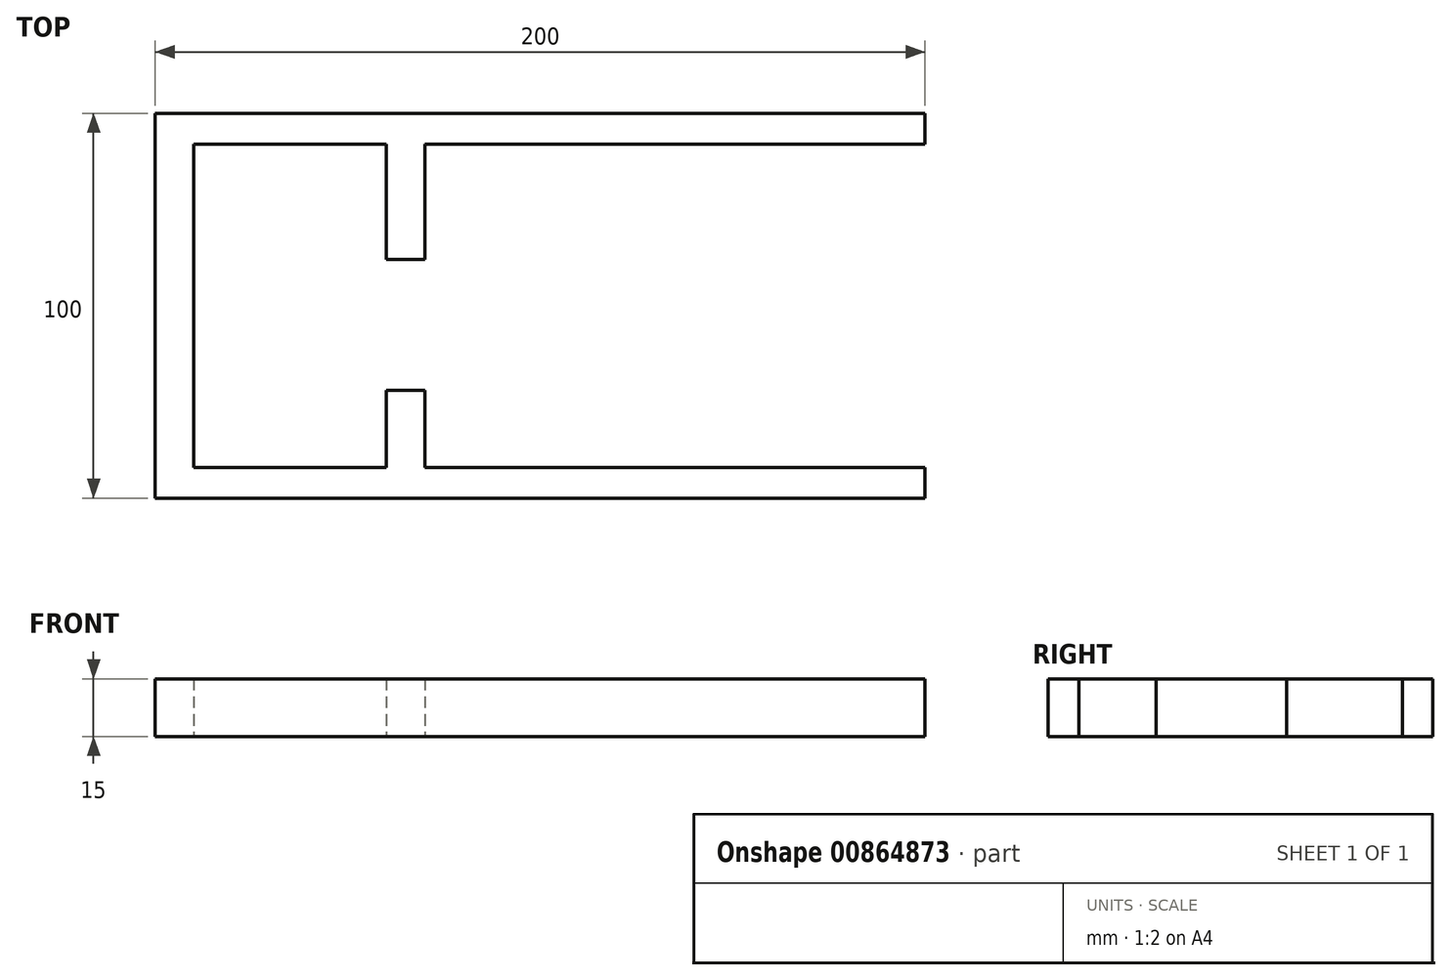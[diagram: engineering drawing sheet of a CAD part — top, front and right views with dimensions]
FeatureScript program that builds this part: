
annotation { "Feature Type Name" : "Feature", "Feature Type Description" : "" }
export const myFeature = defineFeature(function(context is Context, id is Id, definition is map)
    precondition{}
    {
        {
            var Q0;
            Q0=qCreatedBy(makeId("Top.planeOp"),FACE);
            var sketch = newSketch(context, id + "F0", { "sketchPlane" : qUnion([Q0])});
            skLineSegment(sketch, "E0.bottom", {"start": v(100, -50) * mm, "end": v(-100, -50) * mm});
            skLineSegment(sketch, "E0.top", {"start": v(100, 50) * mm, "end": v(-100, 50) * mm});
            skLineSegment(sketch, "E0.left", {"start": v(100, -50) * mm, "end": v(100, 50) * mm});
            skLineSegment(sketch, "E0.right", {"start": v(-100, -50) * mm, "end": v(-100, 50) * mm});
            skPoint(sketch, "E0.middle", {"position": v(0, 0) * mm});
            skLineSegment(sketch, "E1", {"start": v(100, 42) * mm, "end": v(-6.4, 42) * mm});
            skLineSegment(sketch, "E2", {"start": v(-6.4, 42) * mm, "end": v(-30, 42) * mm});
            skLineSegment(sketch, "E3", {"start": v(-30, 42) * mm, "end": v(-30, 12) * mm});
            skLineSegment(sketch, "E4", {"start": v(-30, 12) * mm, "end": v(-40, 12) * mm});
            skLineSegment(sketch, "E5", {"start": v(-40, 12) * mm, "end": v(-40, 42) * mm});
            skLineSegment(sketch, "E6", {"start": v(-40, 42) * mm, "end": v(-90, 42) * mm});
            skLineSegment(sketch, "E7", {"start": v(-90, 42) * mm, "end": v(-90, -42) * mm});
            skLineSegment(sketch, "E8", {"start": v(-90, -42) * mm, "end": v(-40, -42) * mm});
            skLineSegment(sketch, "E9", {"start": v(-40, -42) * mm, "end": v(-40, -22) * mm});
            skLineSegment(sketch, "E10", {"start": v(-40, -22) * mm, "end": v(-30, -22) * mm});
            skLineSegment(sketch, "E11", {"start": v(-30, -22) * mm, "end": v(-30, -42) * mm});
            skLineSegment(sketch, "E12", {"start": v(-30, -42) * mm, "end": v(100, -42) * mm});
            skSolve(sketch);
        }
        {
            var Q0;
            Q0=makeQuery(id+"F0.imprint","IMPRINT",FACE,{"disambiguationData":[TD([[makeQuery(id+"F0.imprint","IMPRINT",EDGE,{"derivedFrom":sQuery(id+"F0.wireOp",EDGE,"k69ZBPvS-VnOV-mxax-5bxI-EintjLL2CQrF.bottom")}),-1.0]])]});
            var Q1;
            Q1=makeQuery(id+"F0.imprint","IMPRINT",FACE,{"disambiguationData":[TD([[makeQuery(id+"F0.imprint","IMPRINT",EDGE,{"derivedFrom":sQuery(id+"F0.wireOp",EDGE,"E0.bottom")}),-1.0]])]});
            extrude(context, id + "F1", {"entities" : qUnion([Q0, Q1]), "depth" : 15 * mm, "offsetDistance" : 25 * mm});
        }
    });
